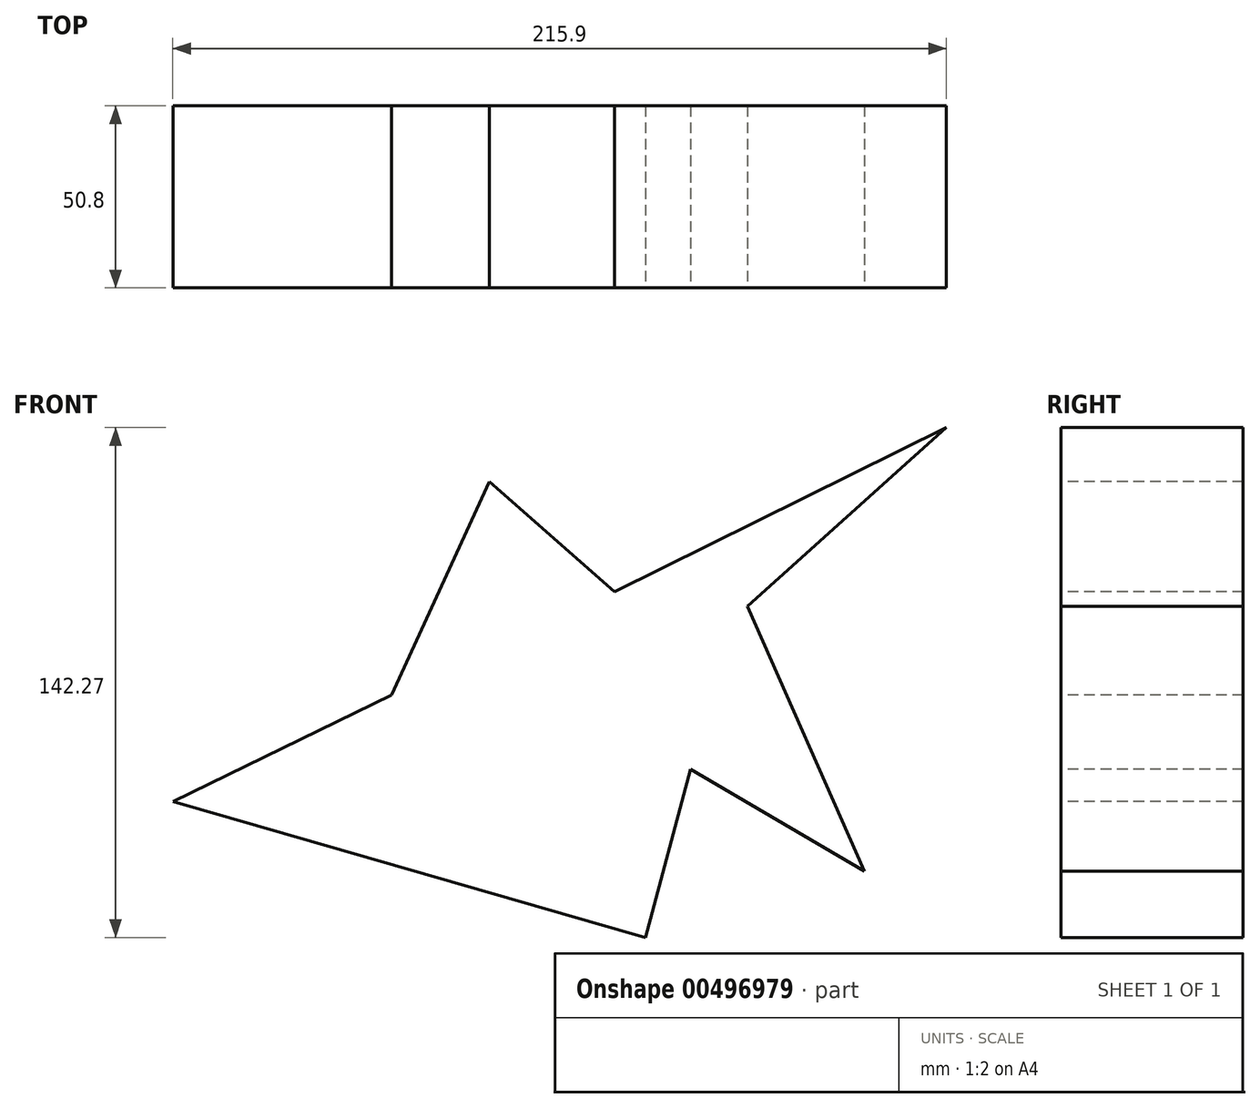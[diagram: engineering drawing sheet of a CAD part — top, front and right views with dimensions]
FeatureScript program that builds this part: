
annotation { "Feature Type Name" : "Feature", "Feature Type Description" : "" }
export const myFeature = defineFeature(function(context is Context, id is Id, definition is map)
    precondition{}
    {
        {
            var Q0;
            Q0=qCreatedBy(makeId("Front.planeOp"),FACE);
            var sketch = newSketch(context, id + "F0", { "sketchPlane" : qUnion([Q0])});
            skLineSegment(sketch, "E0", {"start": v(0, 0) * mm, "end": v(12.54, 46.96) * mm});
            skLineSegment(sketch, "E1", {"start": v(12.54, 46.96) * mm, "end": v(61.06, 18.44) * mm});
            skLineSegment(sketch, "E2", {"start": v(61.06, 18.44) * mm, "end": v(28.35, 92.42) * mm});
            skLineSegment(sketch, "E3", {"start": v(28.35, 92.42) * mm, "end": v(83.96, 142.27) * mm});
            skLineSegment(sketch, "E4", {"start": v(83.96, 142.27) * mm, "end": v(-8.72, 96.43) * mm});
            skLineSegment(sketch, "E5", {"start": v(-8.72, 96.43) * mm, "end": v(-43.62, 127.25) * mm});
            skLineSegment(sketch, "E6", {"start": v(-43.62, 127.25) * mm, "end": v(-70.87, 67.59) * mm});
            skLineSegment(sketch, "E7", {"start": v(-70.87, 67.59) * mm, "end": v(-131.94, 37.97) * mm});
            skLineSegment(sketch, "E8", {"start": v(-131.94, 37.97) * mm, "end": v(0, 0) * mm});
            skSolve(sketch);
        }
        {
            var Q0;
            Q0=makeQuery(id+"F0.imprint","IMPRINT",FACE,{"disambiguationData":[TD([[makeQuery(id+"F0.imprint","IMPRINT",EDGE,{"derivedFrom":sQuery(id+"F0.wireOp",EDGE,"E0")}),1.0]])]});
            extrude(context, id + "F1", {"entities" : qUnion([Q0]), "oppositeDirection" : true, "depth" : 50.8 * mm});
        }
    });
